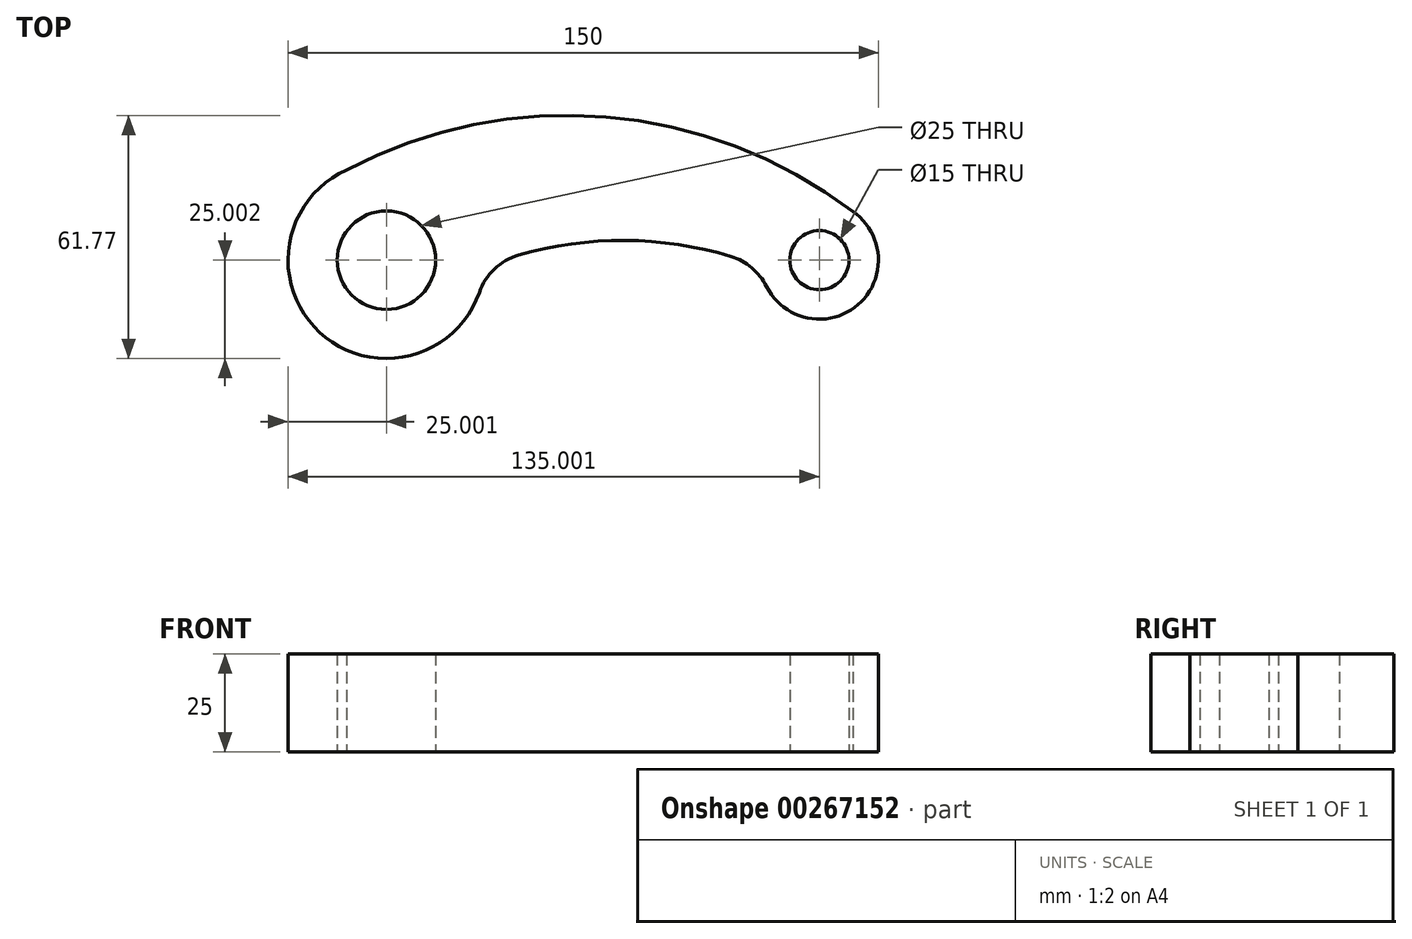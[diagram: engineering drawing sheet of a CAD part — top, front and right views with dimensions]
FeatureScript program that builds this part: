
annotation { "Feature Type Name" : "Feature", "Feature Type Description" : "" }
export const myFeature = defineFeature(function(context is Context, id is Id, definition is map)
    precondition{}
    {
        {
            var Q0;
            Q0=qCreatedBy(makeId("Top.planeOp"),FACE);
            var sketch = newSketch(context, id + "F0", { "sketchPlane" : qUnion([Q0])});
            skCircle(sketch, "E0", {"center": v(-46.77, 25.94) * mm, "radius": 12.5 * mm});
            skCircle(sketch, "E1", {"center": v(63.23, 25.94) * mm, "radius": 7.5 * mm});
            skPoint(sketch, "E2.start.orphan", {"position": v(-46.77, 13.44) * mm});
            skPoint(sketch, "E3", {"position": v(13.23, -64.06) * mm});
            skArc(sketch, "E4", {"start": v(-56.84, 48.82) * mm, "mid": v(-63.73, 7.57) * mm, "end": v(-23.16, 17.72) * mm});
            skArc(sketch, "E5", {"start": v(49.82, 19.23) * mm, "mid": v(73.07, 14.62) * mm, "end": v(71.76, 38.28) * mm});
            skArc(sketch, "E6.trimOffspring", {"start": v(40.75, 26.87) * mm, "mid": v(13.82, 30.94) * mm, "end": v(-13.16, 27.2) * mm});
            skPoint(sketch, "E7", {"position": v(-22.56, 32.16) * mm});
            skPoint(sketch, "E8.visualSharp", {"position": v(-21.83, 24.24) * mm});
            skArc(sketch, "E8.filletArc", {"start": v(-13.16, 27.2) * mm, "mid": v(-19.31, 23.68) * mm, "end": v(-23.16, 17.72) * mm});
            skPoint(sketch, "E9", {"position": v(49.51, 32) * mm});
            skPoint(sketch, "E10.visualSharp", {"position": v(48.33, 24.22) * mm});
            skArc(sketch, "E10.filletArc", {"start": v(49.82, 19.23) * mm, "mid": v(46.07, 23.98) * mm, "end": v(40.75, 26.87) * mm});
            skArc(sketch, "E11", {"start": v(71.76, 38.28) * mm, "mid": v(9, 62.3) * mm, "end": v(-56.84, 48.82) * mm});
            skSolve(sketch);
        }
        {
            var Q0;
            Q0 = qSketchRegion(id + "F0", true);
            extrude(context, id + "F1", {"entities" : qUnion([Q0]), "depth" : 25 * mm});
        }
    });
